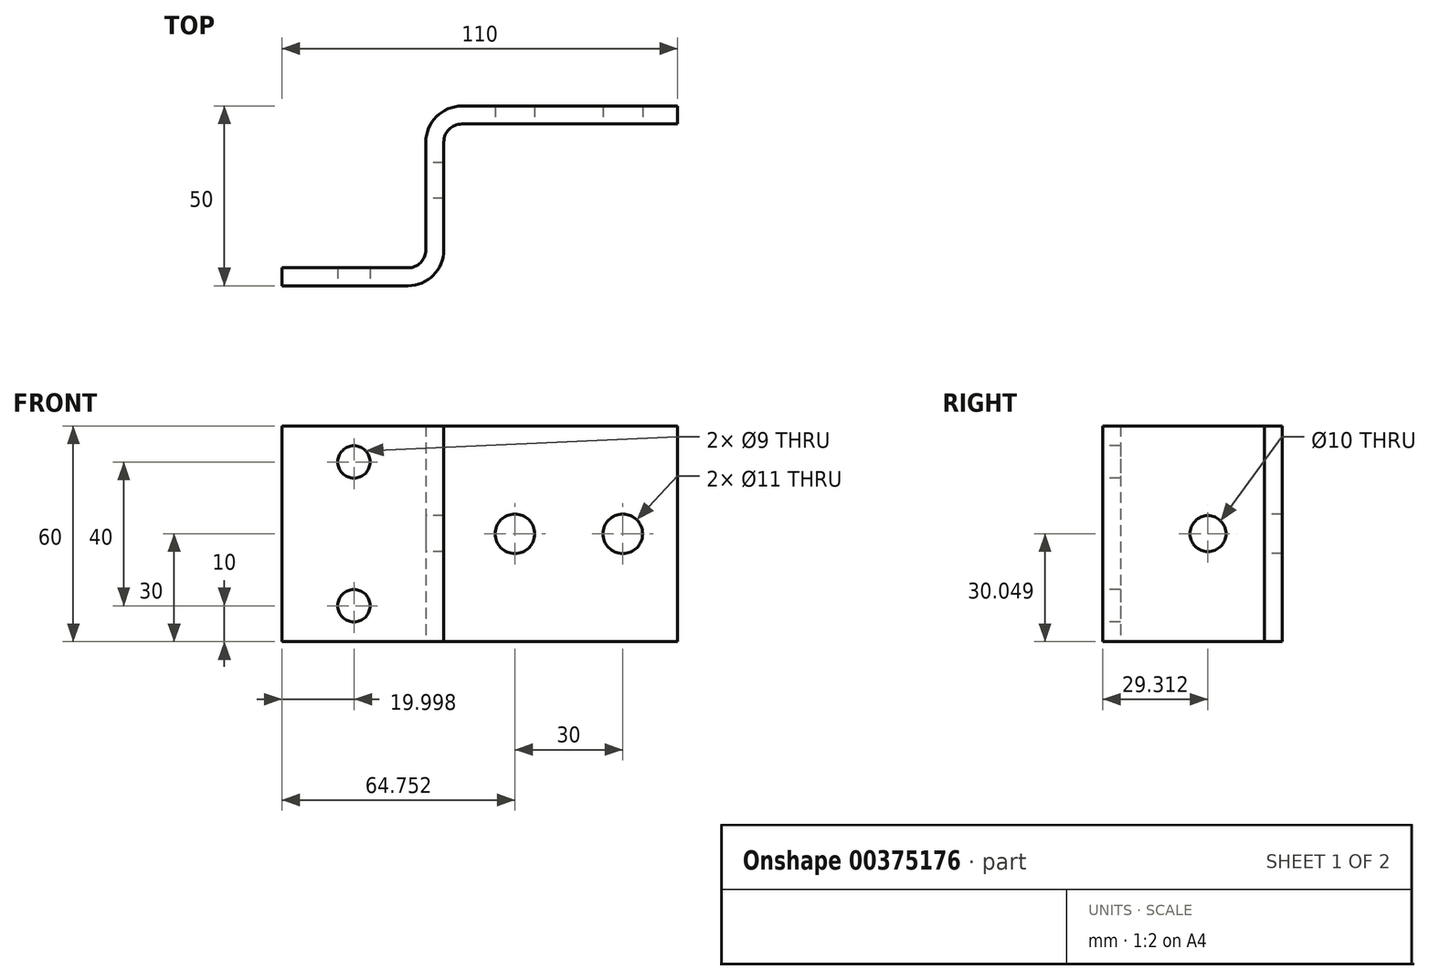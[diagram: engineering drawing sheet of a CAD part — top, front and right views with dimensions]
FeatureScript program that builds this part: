
annotation { "Feature Type Name" : "Feature", "Feature Type Description" : "" }
export const myFeature = defineFeature(function(context is Context, id is Id, definition is map)
    precondition{}
    {
        {
            var Q0;
            Q0=qCreatedBy(makeId("Top.planeOp"),FACE);
            var sketch = newSketch(context, id + "F0", { "sketchPlane" : qUnion([Q0])});
            skLineSegment(sketch, "E0.bottom", {"start": v(-93.54, -9.53) * mm, "end": v(-58.54, -9.53) * mm});
            skLineSegment(sketch, "E0.top", {"start": v(-93.54, -14.53) * mm, "end": v(-58.54, -14.53) * mm});
            skLineSegment(sketch, "E0.left", {"start": v(-93.54, -9.53) * mm, "end": v(-93.54, -14.53) * mm});
            skLineSegment(sketch, "E1.left", {"start": v(-48.54, -4.53) * mm, "end": v(-48.54, 25.47) * mm});
            skLineSegment(sketch, "E1.right", {"start": v(-53.54, -4.53) * mm, "end": v(-53.54, 25.47) * mm});
            skLineSegment(sketch, "E2.bottom", {"start": v(-43.54, 30.47) * mm, "end": v(16.46, 30.47) * mm});
            skLineSegment(sketch, "E2.top", {"start": v(-43.54, 35.47) * mm, "end": v(16.46, 35.47) * mm});
            skLineSegment(sketch, "E2.right", {"start": v(16.46, 35.47) * mm, "end": v(16.46, 30.47) * mm});
            skPoint(sketch, "E3.visualSharp", {"position": v(-48.54, -14.53) * mm});
            skPoint(sketch, "E1.bottom.end.orphan", {"position": v(-53.54, -19.53) * mm});
            skPoint(sketch, "E4.visualSharp", {"position": v(-53.54, -9.53) * mm});
            skArc(sketch, "E4.filletArc", {"start": v(-58.54, -9.53) * mm, "mid": v(-55, -8.07) * mm, "end": v(-53.54, -4.53) * mm});
            skPoint(sketch, "E5.newPointB", {"position": v(-53.54, -14.53) * mm});
            skArc(sketch, "E5.filletArc", {"start": v(-58.54, -14.53) * mm, "mid": v(-51.47, -11.6) * mm, "end": v(-48.54, -4.53) * mm});
            skPoint(sketch, "E6.visualSharp", {"position": v(-48.54, 30.47) * mm});
            skArc(sketch, "E6.filletArc", {"start": v(-43.54, 30.47) * mm, "mid": v(-47.08, 29) * mm, "end": v(-48.54, 25.47) * mm});
            skPoint(sketch, "E7.visualSharp", {"position": v(-53.54, 35.47) * mm});
            skArc(sketch, "E7.filletArc", {"start": v(-43.54, 35.47) * mm, "mid": v(-50.61, 32.54) * mm, "end": v(-53.54, 25.47) * mm});
            skPoint(sketch, "E1.top.start.orphan", {"position": v(-48.54, 35.47) * mm});
            skPoint(sketch, "E2.left.start.orphan", {"position": v(-53.54, 30.47) * mm});
            skLineSegment(sketch, "E8", {"start": v(-93.54, -14.53) * mm, "end": v(-73.95, -14.53) * mm});
            skSolve(sketch);
        }
        {
            var Q0;
            Q0 = qSketchRegion(id + "F0", true);
            extrude(context, id + "F1", {"entities" : qUnion([Q0]), "depth" : 60 * mm});
        }
        {
            var Q0;
            Q0=makeQuery(id+"F1.opExtrude","SWEPT_FACE",FACE,{"disambiguationData":[OSD([sQuery(id+"F0.wireOp",EDGE,"E1.right")])]});
            var sketch = newSketch(context, id + "F2", { "sketchPlane" : qUnion([Q0])});
            skPoint(sketch, "E9", {"position": v(-46.74, 60.05) * mm});
            skPoint(sketch, "E10", {"position": v(-21.7, 60) * mm});
            skPoint(sketch, "E11", {"position": v(-46.74, 30.05) * mm});
            skPoint(sketch, "E12", {"position": v(-41.7, 60.27) * mm});
            skPoint(sketch, "E13", {"position": v(-34.78, 60.03) * mm});
            skPoint(sketch, "E14", {"position": v(-14.78, 60) * mm});
            skPoint(sketch, "E15", {"position": v(-14.78, 30.05) * mm});
            skCircle(sketch, "E16", {"center": v(-14.78, 30.05) * mm, "radius": 5 * mm});
            skSolve(sketch);
        }
        {
            var Q0;
            Q0 = qSketchRegion(id + "F2", true);
            extrude(context, id + "F3", {"entities" : qUnion([Q0]), "operationType" : NewBodyOperationType.REMOVE, "oppositeDirection" : true, "depth" : 25 * mm});
        }
        {
            var Q0;
            Q0=makeQuery(id+"F1.opExtrude","SWEPT_FACE",FACE,{"disambiguationData":[OSD([sQuery(id+"F0.wireOp",EDGE,"E0.top"),sQuery(id+"F0.wireOp",EDGE,"E8")])]});
            var sketch = newSketch(context, id + "F4", { "sketchPlane" : qUnion([Q0])});
            skPoint(sketch, "E17", {"position": v(-93.54, 60) * mm});
            skPoint(sketch, "E18", {"position": v(-73.54, 60) * mm});
            skPoint(sketch, "E19", {"position": v(-93.54, 50) * mm});
            skPoint(sketch, "E20", {"position": v(-28.54, 60) * mm});
            skPoint(sketch, "E21", {"position": v(1.46, 60) * mm});
            skPoint(sketch, "E22", {"position": v(16.35, 30) * mm});
            skPoint(sketch, "E23", {"position": v(-93.54, 10) * mm});
            skPoint(sketch, "E24", {"position": v(-73.54, 0) * mm});
            skPoint(sketch, "E25", {"position": v(-93.54, 0) * mm});
            skPoint(sketch, "E26", {"position": v(-73.54, 50) * mm});
            skPoint(sketch, "E27", {"position": v(-73.54, 10) * mm});
            skCircle(sketch, "E28", {"center": v(-73.54, 50) * mm, "radius": 4.5 * mm});
            skCircle(sketch, "E29", {"center": v(-73.54, 10) * mm, "radius": 4.5 * mm});
            skPoint(sketch, "E30", {"position": v(-53.58, 60) * mm});
            skPoint(sketch, "E31", {"position": v(1.46, 30) * mm});
            skPoint(sketch, "E32", {"position": v(-28.54, 30) * mm});
            skCircle(sketch, "E33", {"center": v(-28.54, 30) * mm, "radius": 5.5 * mm});
            skCircle(sketch, "E34", {"center": v(1.46, 30) * mm, "radius": 5.5 * mm});
            skSolve(sketch);
        }
        {
            var Q0;
            Q0 = qSketchRegion(id + "F4", true);
            extrude(context, id + "F5", {"entities" : qUnion([Q0]), "operationType" : NewBodyOperationType.REMOVE, "oppositeDirection" : true, "depth" : 25 * mm});
        }
        {
            var Q0;
            Q0=makeQuery(id+"F4.imprint","IMPRINT",FACE,{"disambiguationData":[TD([[makeQuery(id+"F4.imprint","IMPRINT",EDGE,{"derivedFrom":sQuery(id+"F4.wireOp",EDGE,"E33")}),1.0]])]});
            var Q1;
            Q1=makeQuery(id+"F4.imprint","IMPRINT",FACE,{"disambiguationData":[TD([[makeQuery(id+"F4.imprint","IMPRINT",EDGE,{"derivedFrom":sQuery(id+"F4.wireOp",EDGE,"E34")}),1.0]])]});
            extrude(context, id + "F6", {"entities" : qUnion([Q0, Q1]), "operationType" : NewBodyOperationType.REMOVE, "oppositeDirection" : true, "depth" : 25 * mm});
        }
        {
            var Q0;
            Q0=makeQuery(id+"F1.opExtrude","SWEPT_FACE",FACE,{"disambiguationData":[OSD([sQuery(id+"F0.wireOp",EDGE,"E2.bottom")])]});
            var sketch = newSketch(context, id + "F7", { "sketchPlane" : qUnion([Q0])});
            skPoint(sketch, "E35", {"position": v(16.46, 60) * mm});
            skPoint(sketch, "E36", {"position": v(16.46, 30) * mm});
            skPoint(sketch, "E37", {"position": v(1.21, 60) * mm});
            skPoint(sketch, "E38", {"position": v(-28.79, 60) * mm});
            skPoint(sketch, "E39", {"position": v(-73.79, 60) * mm});
            skPoint(sketch, "E40", {"position": v(1.21, 30) * mm});
            skPoint(sketch, "E41", {"position": v(-28.79, 30) * mm});
            skCircle(sketch, "E42", {"center": v(-28.79, 30) * mm, "radius": 5.5 * mm});
            skCircle(sketch, "E43", {"center": v(1.21, 30) * mm, "radius": 5.5 * mm});
            skSolve(sketch);
        }
        {
            var Q0;
            Q0 = qSketchRegion(id + "F7", true);
            extrude(context, id + "F8", {"entities" : qUnion([Q0]), "operationType" : NewBodyOperationType.REMOVE, "oppositeDirection" : true, "depth" : 25 * mm});
        }
    });
